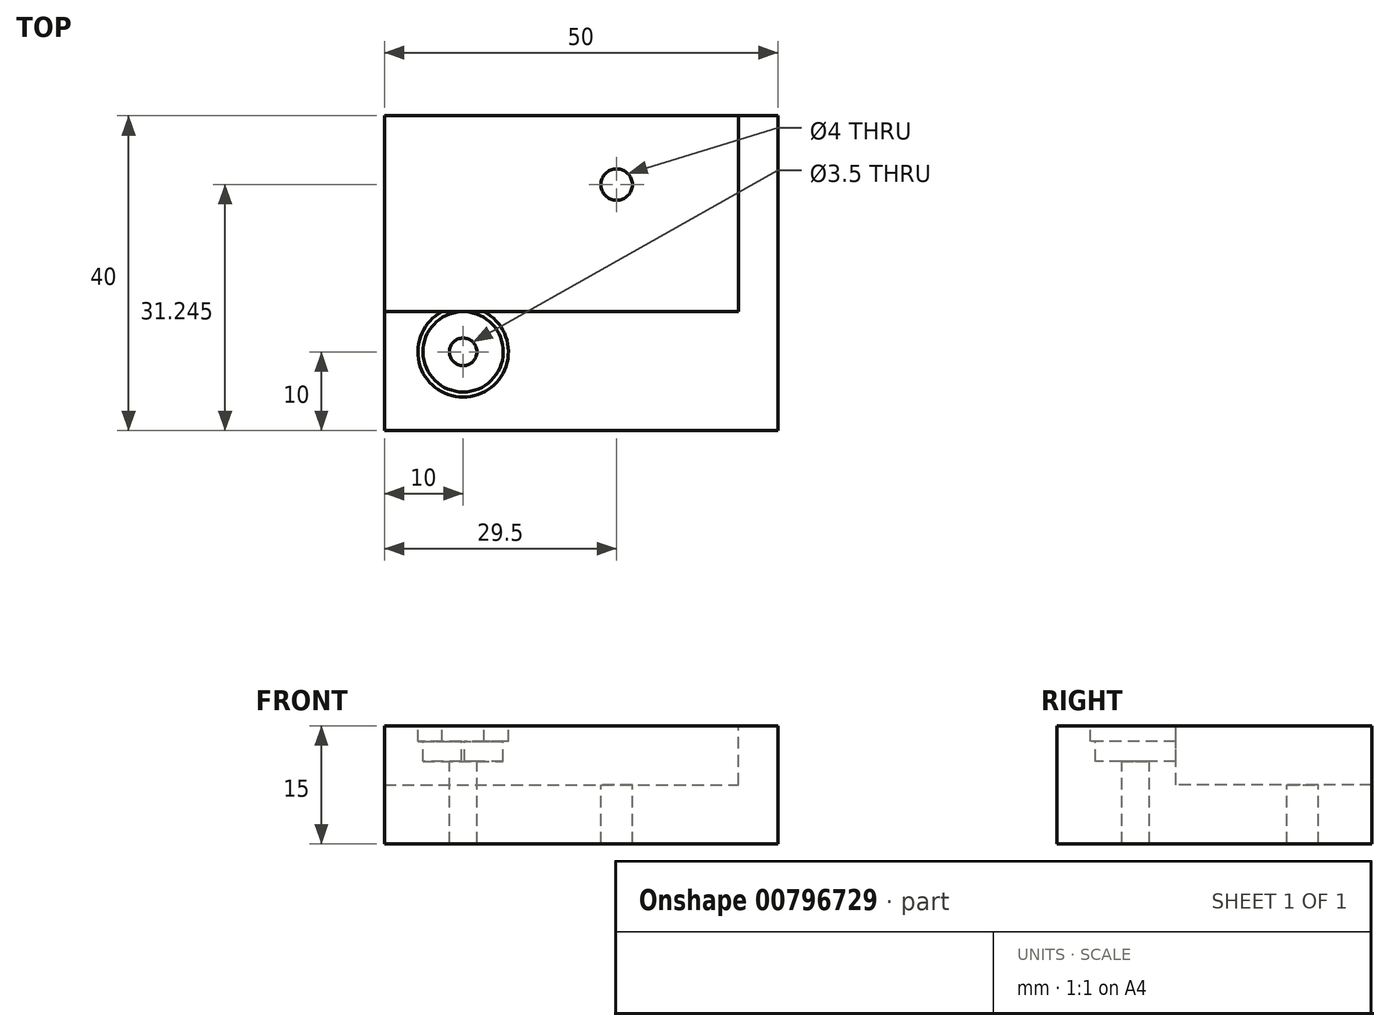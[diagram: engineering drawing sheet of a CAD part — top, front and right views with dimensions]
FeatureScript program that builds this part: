
annotation { "Feature Type Name" : "Feature", "Feature Type Description" : "" }
export const myFeature = defineFeature(function(context is Context, id is Id, definition is map)
    precondition{}
    {
        {
            var Q0;
            Q0=qCreatedBy(makeId("Top.planeOp"),FACE);
            var sketch = newSketch(context, id + "F0", { "sketchPlane" : qUnion([Q0])});
            skLineSegment(sketch, "E0.bottom", {"start": v(0, 0) * mm, "end": v(50, 0) * mm});
            skLineSegment(sketch, "E0.top", {"start": v(0, -40) * mm, "end": v(50, -40) * mm});
            skLineSegment(sketch, "E0.left", {"start": v(0, 0) * mm, "end": v(0, -40) * mm});
            skLineSegment(sketch, "E0.right", {"start": v(50, 0) * mm, "end": v(50, -40) * mm});
            skSolve(sketch);
        }
        {
            var Q0;
            Q0 = qSketchRegion(id + "F0", true);
            extrude(context, id + "F1", {"entities" : qUnion([Q0]), "depth" : 15 * mm, "offsetDistance" : 25 * mm});
        }
        {
            var Q0;
            Q0=makeQuery(id+"F1.opExtrude","CAP_FACE",FACE,{"disambiguationData":[OSD([sQuery(id+"F0.wireOp",EDGE,"E0.bottom"),sQuery(id+"F0.wireOp",EDGE,"E0.top"),sQuery(id+"F0.wireOp",EDGE,"E0.left"),sQuery(id+"F0.wireOp",EDGE,"E0.right")])],"isStart":false});
            var sketch = newSketch(context, id + "F2", { "sketchPlane" : qUnion([Q0])});
            skLineSegment(sketch, "E1", {"start": v(-27.43, -40) * mm, "end": v(54.31, -40) * mm, "construction": true});
            skLineSegment(sketch, "E2.0", {"start": v(-27.43, -30) * mm, "end": v(54.31, -30) * mm, "construction": true});
            skLineSegment(sketch, "E3", {"start": v(0, -52.28) * mm, "end": v(0, 12.41) * mm, "construction": true});
            skLineSegment(sketch, "E4.0", {"start": v(10, -52.28) * mm, "end": v(10, 12.41) * mm, "construction": true});
            skCircle(sketch, "E5", {"center": v(10, -30) * mm, "radius": 5.75 * mm});
            skSolve(sketch);
        }
        {
            var Q0;
            Q0 = qSketchRegion(id + "F2", true);
            extrude(context, id + "F3", {"entities" : qUnion([Q0]), "operationType" : NewBodyOperationType.REMOVE, "oppositeDirection" : true, "depth" : 2 * mm, "offsetDistance" : 25 * mm});
        }
        {
            var Q0;
            Q0=makeQuery(id+"F1.opExtrude","CAP_FACE",FACE,{"disambiguationData":[OSD([sQuery(id+"F0.wireOp",EDGE,"E0.bottom"),sQuery(id+"F0.wireOp",EDGE,"E0.top"),sQuery(id+"F0.wireOp",EDGE,"E0.left"),sQuery(id+"F0.wireOp",EDGE,"E0.right")])],"isStart":false});
            var sketch = newSketch(context, id + "F4", { "sketchPlane" : qUnion([Q0])});
            skLineSegment(sketch, "E6", {"start": v(50, 10.52) * mm, "end": v(50, -53.09) * mm, "construction": true});
            skLineSegment(sketch, "E7.0", {"start": v(29.5, 10.52) * mm, "end": v(29.5, -53.09) * mm, "construction": true});
            skLineSegment(sketch, "E8", {"start": v(9.76, -24.26) * mm, "end": v(61.17, -24.26) * mm, "construction": true});
            skLineSegment(sketch, "E9.0", {"start": v(9.76, -8.76) * mm, "end": v(61.17, -8.76) * mm, "construction": true});
            skCircle(sketch, "E10", {"center": v(29.5, -8.76) * mm, "radius": 2 * mm});
            skSolve(sketch);
        }
        {
            var Q0;
            Q0 = qSketchRegion(id + "F4", true);
            extrude(context, id + "F5", {"entities" : qUnion([Q0]), "operationType" : NewBodyOperationType.REMOVE, "endBound" : BoundingType.THROUGH_ALL, "oppositeDirection" : true, "depth" : 25 * mm, "offsetDistance" : 25 * mm});
        }
        {
            var Q0;
            Q0=makeQuery(id+"F1.opExtrude","CAP_FACE",FACE,{"disambiguationData":[OSD([sQuery(id+"F0.wireOp",EDGE,"E0.bottom"),sQuery(id+"F0.wireOp",EDGE,"E0.top"),sQuery(id+"F0.wireOp",EDGE,"E0.left"),sQuery(id+"F0.wireOp",EDGE,"E0.right")])],"isStart":false});
            var sketch = newSketch(context, id + "F6", { "sketchPlane" : qUnion([Q0])});
            skLineSegment(sketch, "E11", {"start": v(45, 9.33) * mm, "end": v(45, -54.28) * mm, "construction": true});
            skLineSegment(sketch, "E12.0", {"start": v(29.5, 9.33) * mm, "end": v(29.5, -54.28) * mm, "construction": true});
            skLineSegment(sketch, "E13", {"start": v(6.58, -24.9) * mm, "end": v(58, -24.9) * mm, "construction": true});
            skLineSegment(sketch, "E14.0", {"start": v(6.58, -9.4) * mm, "end": v(58, -9.4) * mm, "construction": true});
            skLineSegment(sketch, "E15", {"start": v(45, 0) * mm, "end": v(45, -24.9) * mm});
            skLineSegment(sketch, "E16", {"start": v(45, -24.9) * mm, "end": v(0, -24.9) * mm});
            skLineSegment(sketch, "E17", {"start": v(0, -24.9) * mm, "end": v(0, 0) * mm});
            skLineSegment(sketch, "E18", {"start": v(0, 0) * mm, "end": v(45, 0) * mm});
            skSolve(sketch);
        }
        {
            var Q0;
            Q0 = qSketchRegion(id + "F6", true);
            extrude(context, id + "F7", {"entities" : qUnion([Q0]), "operationType" : NewBodyOperationType.REMOVE, "oppositeDirection" : true, "depth" : 7.5 * mm, "offsetDistance" : 25 * mm});
        }
        {
            var Q0;
            Q0=makeQuery(id+"F3.boolean.opBoolean","COPY",FACE,{"derivedFrom":makeQuery(id+"F3.opExtrude","CAP_FACE",FACE,{"disambiguationData":[OSD([sQuery(id+"F2.wireOp",EDGE,"E5")])],"isStart":false})});
            var sketch = newSketch(context, id + "F8", { "sketchPlane" : qUnion([Q0])});
            skCircle(sketch, "E19", {"center": v(10, -30) * mm, "radius": 5.1 * mm});
            skSolve(sketch);
        }
        {
            var Q0;
            Q0 = qSketchRegion(id + "F8", true);
            extrude(context, id + "F9", {"entities" : qUnion([Q0]), "operationType" : NewBodyOperationType.REMOVE, "oppositeDirection" : true, "depth" : 2.5 * mm, "offsetDistance" : 25 * mm});
        }
        {
            var Q0;
            Q0=makeQuery(id+"F1.opExtrude","CAP_FACE",FACE,{"disambiguationData":[OSD([sQuery(id+"F0.wireOp",EDGE,"E0.bottom"),sQuery(id+"F0.wireOp",EDGE,"E0.top"),sQuery(id+"F0.wireOp",EDGE,"E0.left"),sQuery(id+"F0.wireOp",EDGE,"E0.right")])],"isStart":false});
            var sketch = newSketch(context, id + "F10", { "sketchPlane" : qUnion([Q0])});
            skCircle(sketch, "E20", {"center": v(10, -30) * mm, "radius": 1.75 * mm});
            skSolve(sketch);
        }
        {
            var Q0;
            Q0 = qSketchRegion(id + "F10", true);
            extrude(context, id + "F11", {"entities" : qUnion([Q0]), "operationType" : NewBodyOperationType.REMOVE, "endBound" : BoundingType.THROUGH_ALL, "oppositeDirection" : true, "depth" : 25 * mm, "offsetDistance" : 25 * mm});
        }
    });
